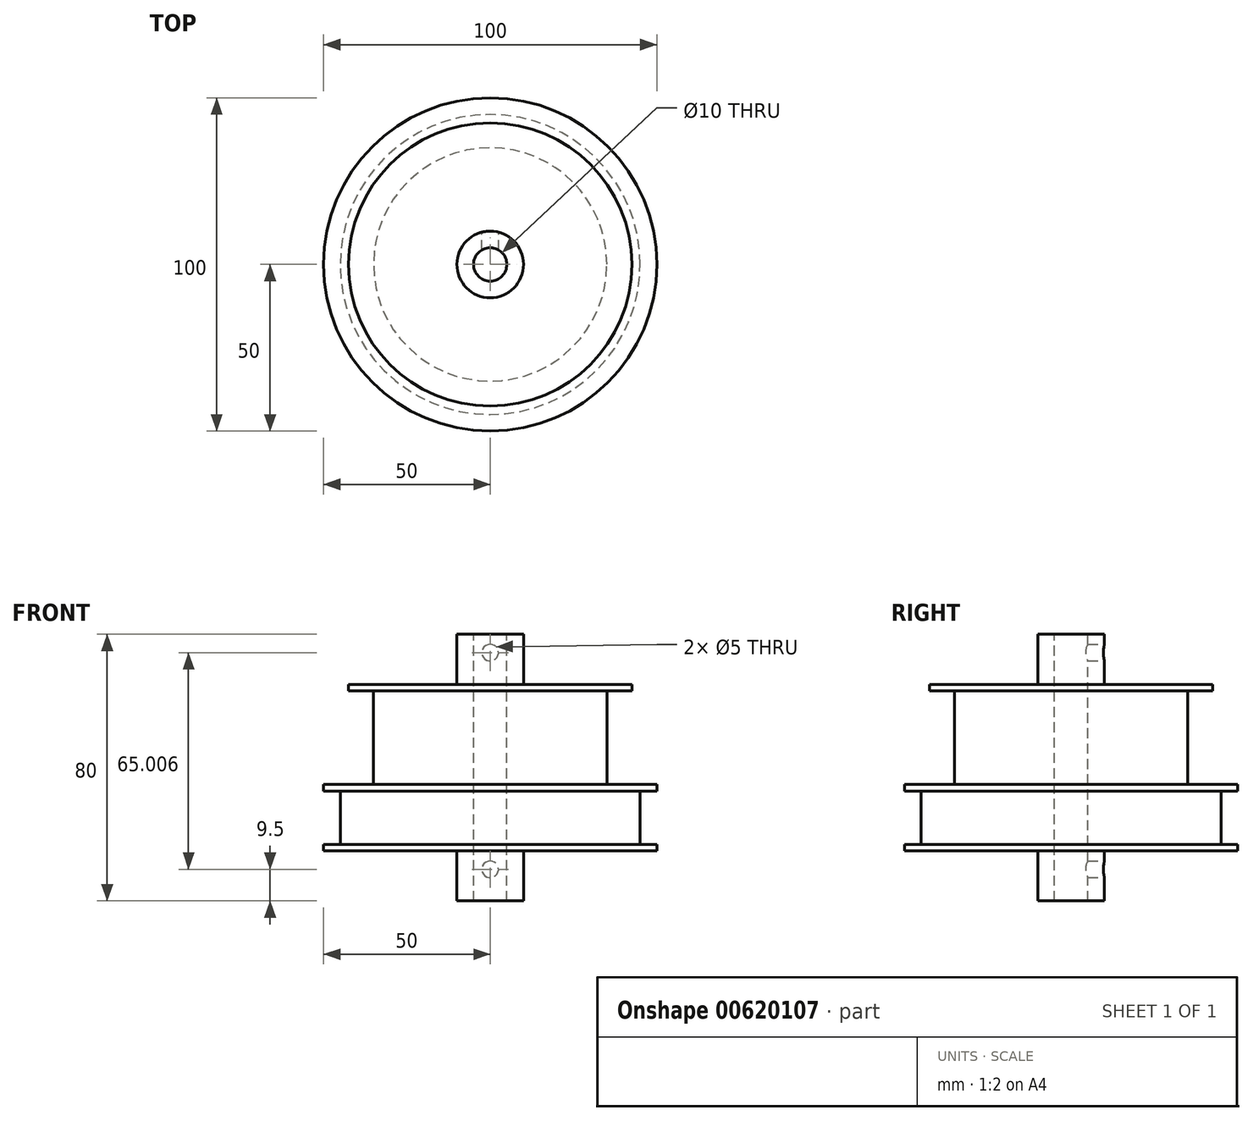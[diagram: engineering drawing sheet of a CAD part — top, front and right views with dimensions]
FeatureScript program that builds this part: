
annotation { "Feature Type Name" : "Feature", "Feature Type Description" : "" }
export const myFeature = defineFeature(function(context is Context, id is Id, definition is map)
    precondition{}
    {
        {
            var Q0;
            Q0=qCreatedBy(makeId("Top.planeOp"),FACE);
            var sketch = newSketch(context, id + "F0", { "sketchPlane" : qUnion([Q0])});
            skCircle(sketch, "E0", {"center": v(0, 0) * mm, "radius": 50 * mm});
            skSolve(sketch);
        }
        {
            var Q0;
            Q0=makeQuery(id+"F0.imprint","IMPRINT",FACE,{"disambiguationData":[TD([[makeQuery(id+"F0.imprint","IMPRINT",EDGE,{"derivedFrom":sQuery(id+"F0.wireOp",EDGE,"E0")}),1.0]])]});
            extrude(context, id + "F1", {"entities" : qUnion([Q0]), "depth" : 2 * mm, "offsetDistance" : 25 * mm});
        }
        {
            var Q0;
            Q0=makeQuery(id+"F1.opExtrude","CAP_FACE",FACE,{"disambiguationData":[OSD([sQuery(id+"F0.wireOp",EDGE,"E0")])],"isStart":false});
            var sketch = newSketch(context, id + "F2", { "sketchPlane" : qUnion([Q0])});
            skCircle(sketch, "E1", {"center": v(0, 0) * mm, "radius": 45 * mm});
            skSolve(sketch);
        }
        {
            var Q0;
            Q0=qSketchRegion(id+"F2",true);
            extrude(context, id + "F3", {"entities" : qUnion([Q0]), "operationType" : NewBodyOperationType.ADD, "depth" : 16 * mm, "offsetDistance" : 25 * mm});
        }
        {
            var Q0;
            Q0=makeQuery(id+"F3.opExtrude","CAP_FACE",FACE,{"disambiguationData":[OSD([sQuery(id+"F2.wireOp",EDGE,"E1")])],"isStart":false});
            var sketch = newSketch(context, id + "F4", { "sketchPlane" : qUnion([Q0])});
            skCircle(sketch, "E2", {"center": v(0, 0) * mm, "radius": 50 * mm});
            skSolve(sketch);
        }
        {
            var Q0;
            Q0=makeQuery(id+"F4.imprint","IMPRINT",FACE,{"disambiguationData":[TD([[makeQuery(id+"F4.imprint","IMPRINT",EDGE,{"derivedFrom":makeQuery(id+"F3.opExtrude","CAP_EDGE",EDGE,{"disambiguationData":[OSD([sQuery(id+"F2.wireOp",EDGE,"E1")])],"isStart":false})}),1.0]])]});
            var Q1;
            Q1=makeQuery(id+"F4.imprint","IMPRINT",FACE,{"disambiguationData":[TD([[makeQuery(id+"F4.imprint","IMPRINT",EDGE,{"derivedFrom":sQuery(id+"F4.wireOp",EDGE,"E2")}),1.0]])]});
            extrude(context, id + "F5", {"entities" : qUnion([Q0, Q1]), "operationType" : NewBodyOperationType.ADD, "depth" : 2 * mm, "offsetDistance" : 25 * mm});
        }
        {
            var Q0;
            Q0=makeQuery(id+"F5.opExtrude","CAP_FACE",FACE,{"disambiguationData":[OSD([sQuery(id+"F4.wireOp",EDGE,"E2")])],"isStart":false});
            var sketch = newSketch(context, id + "F6", { "sketchPlane" : qUnion([Q0])});
            skCircle(sketch, "E3", {"center": v(0, 0) * mm, "radius": 10 * mm});
            skSolve(sketch);
        }
        {
            var Q0;
            Q0=makeQuery(id+"F6.imprint","IMPRINT",FACE,{"disambiguationData":[TD([[makeQuery(id+"F6.imprint","IMPRINT",EDGE,{"derivedFrom":sQuery(id+"F6.wireOp",EDGE,"E3")}),1.0]])]});
            extrude(context, id + "F7", {"entities" : qUnion([Q0]), "operationType" : NewBodyOperationType.ADD, "depth" : 45 * mm, "offsetDistance" : 25 * mm});
        }
        {
            var Q0;
            Q0=makeQuery(id+"F1.opExtrude","CAP_FACE",FACE,{"disambiguationData":[OSD([sQuery(id+"F0.wireOp",EDGE,"E0")])],"isStart":true});
            var sketch = newSketch(context, id + "F8", { "sketchPlane" : qUnion([Q0])});
            skCircle(sketch, "E4", {"center": v(0, 0) * mm, "radius": 10 * mm});
            skSolve(sketch);
        }
        {
            var Q0;
            Q0=makeQuery(id+"F8.imprint","IMPRINT",FACE,{"disambiguationData":[TD([[makeQuery(id+"F8.imprint","IMPRINT",EDGE,{"derivedFrom":sQuery(id+"F8.wireOp",EDGE,"E4")}),1.0]])]});
            extrude(context, id + "F9", {"entities" : qUnion([Q0]), "operationType" : NewBodyOperationType.ADD, "depth" : 15 * mm, "offsetDistance" : 25 * mm});
        }
        {
            var Q0;
            Q0=makeQuery(id+"F7.opExtrude","CAP_FACE",FACE,{"disambiguationData":[OSD([sQuery(id+"F6.wireOp",EDGE,"E3")])],"isStart":false});
            var sketch = newSketch(context, id + "F10", { "sketchPlane" : qUnion([Q0])});
            skCircle(sketch, "E5", {"center": v(0, 0) * mm, "radius": 5 * mm});
            skSolve(sketch);
        }
        {
            var Q0;
            Q0=makeQuery(id+"F10.imprint","IMPRINT",FACE,{"disambiguationData":[TD([[makeQuery(id+"F10.imprint","IMPRINT",EDGE,{"derivedFrom":sQuery(id+"F10.wireOp",EDGE,"E5")}),1.0]])]});
            extrude(context, id + "F11", {"entities" : qUnion([Q0]), "operationType" : NewBodyOperationType.REMOVE, "endBound" : BoundingType.THROUGH_ALL, "oppositeDirection" : true, "depth" : 25 * mm, "offsetDistance" : 25 * mm});
        }
        {
            var Q0;
            Q0=makeQuery(id+"F7.opExtrude","CAP_FACE",FACE,{"disambiguationData":[OSD([sQuery(id+"F6.wireOp",EDGE,"E3")])],"isStart":false});
            var sketch = newSketch(context, id + "F12", { "sketchPlane" : qUnion([Q0])});
            skLineSegment(sketch, "E6", {"start": v(-26.54, 10) * mm, "end": v(26.01, 10) * mm});
            skSolve(sketch);
        }
        {
            var Q0;
            Q0=sQuery(id+"F12.wireOp",EDGE,"E6");
            extrude(context, id + "F13", {"bodyType" : ToolBodyType.SURFACE, "surfaceEntities" : qUnion([Q0]), "oppositeDirection" : true, "depth" : 60 * mm, "offsetDistance" : 25 * mm});
        }
        {
            var Q0;
            Q0=makeQuery(id+"F13.opExtrude","SWEPT_FACE",FACE,{"disambiguationData":[OSD([sQuery(id+"F12.wireOp",EDGE,"E6")])]});
            var sketch = newSketch(context, id + "F14", { "sketchPlane" : qUnion([Q0])});
            skCircle(sketch, "E7", {"center": v(0, 59.5) * mm, "radius": 2.5 * mm});
            skCircle(sketch, "E8", {"center": v(0, -5.5) * mm, "radius": 2.5 * mm});
            skSolve(sketch);
        }
        {
            var Q0;
            Q0=makeQuery(id+"F14.imprint","IMPRINT",FACE,{"disambiguationData":[TD([[makeQuery(id+"F14.imprint","IMPRINT",EDGE,{"derivedFrom":sQuery(id+"F14.wireOp",EDGE,"E7")}),1.0]])]});
            var Q1;
            Q1=makeQuery(id+"F14.imprint","IMPRINT",FACE,{"disambiguationData":[TD([[makeQuery(id+"F14.imprint","IMPRINT",EDGE,{"derivedFrom":sQuery(id+"F14.wireOp",EDGE,"E8")}),1.0]])]});
            var Q2;
            Q2=makeQuery(id+"F11.boolean.opBoolean","COPY",FACE,{"derivedFrom":makeQuery(id+"F11.opExtrude","SWEPT_FACE",FACE,{"disambiguationData":[OSD([sQuery(id+"F10.wireOp",EDGE,"E5")])]})});
            extrude(context, id + "F15", {"entities" : qUnion([Q0, Q1]), "operationType" : NewBodyOperationType.REMOVE, "endBound" : BoundingType.UP_TO_SURFACE, "oppositeDirection" : true, "depth" : 25 * mm, "endBoundEntityFace" : qUnion([Q2]), "offsetDistance" : 25 * mm});
        }
        {
            var Q0;
            Q0=makeQuery(id+"F5.opExtrude","CAP_FACE",FACE,{"disambiguationData":[OSD([sQuery(id+"F4.wireOp",EDGE,"E2")])],"isStart":false});
            var sketch = newSketch(context, id + "F16", { "sketchPlane" : qUnion([Q0])});
            skCircle(sketch, "E9", {"center": v(0, 0) * mm, "radius": 35 * mm});
            skSolve(sketch);
        }
        {
            var Q0;
            Q0=makeQuery(id+"F16.imprint","IMPRINT",FACE,{"disambiguationData":[TD([[makeQuery(id+"F16.imprint","IMPRINT",EDGE,{"derivedFrom":sQuery(id+"F16.wireOp",EDGE,"E9")}),1.0]])]});
            extrude(context, id + "F17", {"entities" : qUnion([Q0]), "operationType" : NewBodyOperationType.ADD, "depth" : 30 * mm, "offsetDistance" : 25 * mm});
        }
        {
            var Q0;
            Q0=makeQuery(id+"F17.opExtrude","CAP_FACE",FACE,{"disambiguationData":[OSD([sQuery(id+"F6.wireOp",EDGE,"E3"),sQuery(id+"F16.wireOp",EDGE,"E9")])],"isStart":false});
            var sketch = newSketch(context, id + "F18", { "sketchPlane" : qUnion([Q0])});
            skCircle(sketch, "E10", {"center": v(0, 0) * mm, "radius": 42.5 * mm});
            skSolve(sketch);
        }
        {
            var Q0;
            Q0=makeQuery(id+"F18.imprint","IMPRINT",FACE,{"disambiguationData":[TD([[makeQuery(id+"F18.imprint","IMPRINT",EDGE,{"derivedFrom":sQuery(id+"F18.wireOp",EDGE,"E10")}),1.0]])]});
            extrude(context, id + "F19", {"entities" : qUnion([Q0]), "operationType" : NewBodyOperationType.ADD, "oppositeDirection" : true, "depth" : 2 * mm, "offsetDistance" : 25 * mm});
        }
    });
